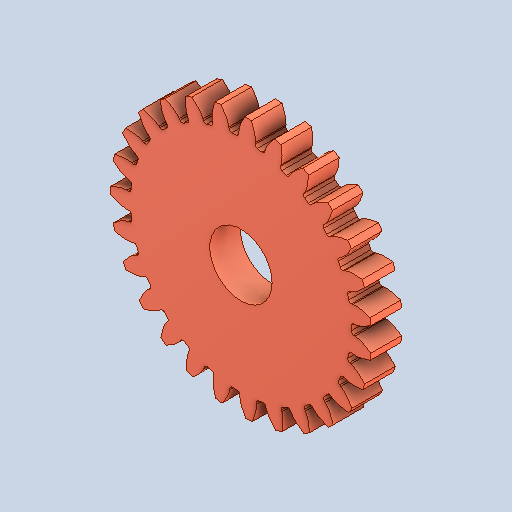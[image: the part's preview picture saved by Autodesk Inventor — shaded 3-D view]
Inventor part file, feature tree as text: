
AUTODESK INVENTOR PART (.ipt)
format: ipt  version: 2022 (Build 260153000, 153)  size: 460,800 bytes
history: imported  units: in
note: dims shown in document units (in); Inventor stores cm internally (conversion verified against a paired STEP export)
features: imported_body x1
ambient origin geometry x8: Origin, YZ Plane, XZ Plane, XY Plane, X Axis, Y Axis, Z Axis, Center Point
bodies: Solid1 (imported_parasolid), Body1 (imported_parasolid)
feature tree (1):
  imported_body  NMx_Import_Brep_tag  [imported B-rep: ~17 faces, bbox_mm=[14.641861, 8.264478, 3.1242]]
